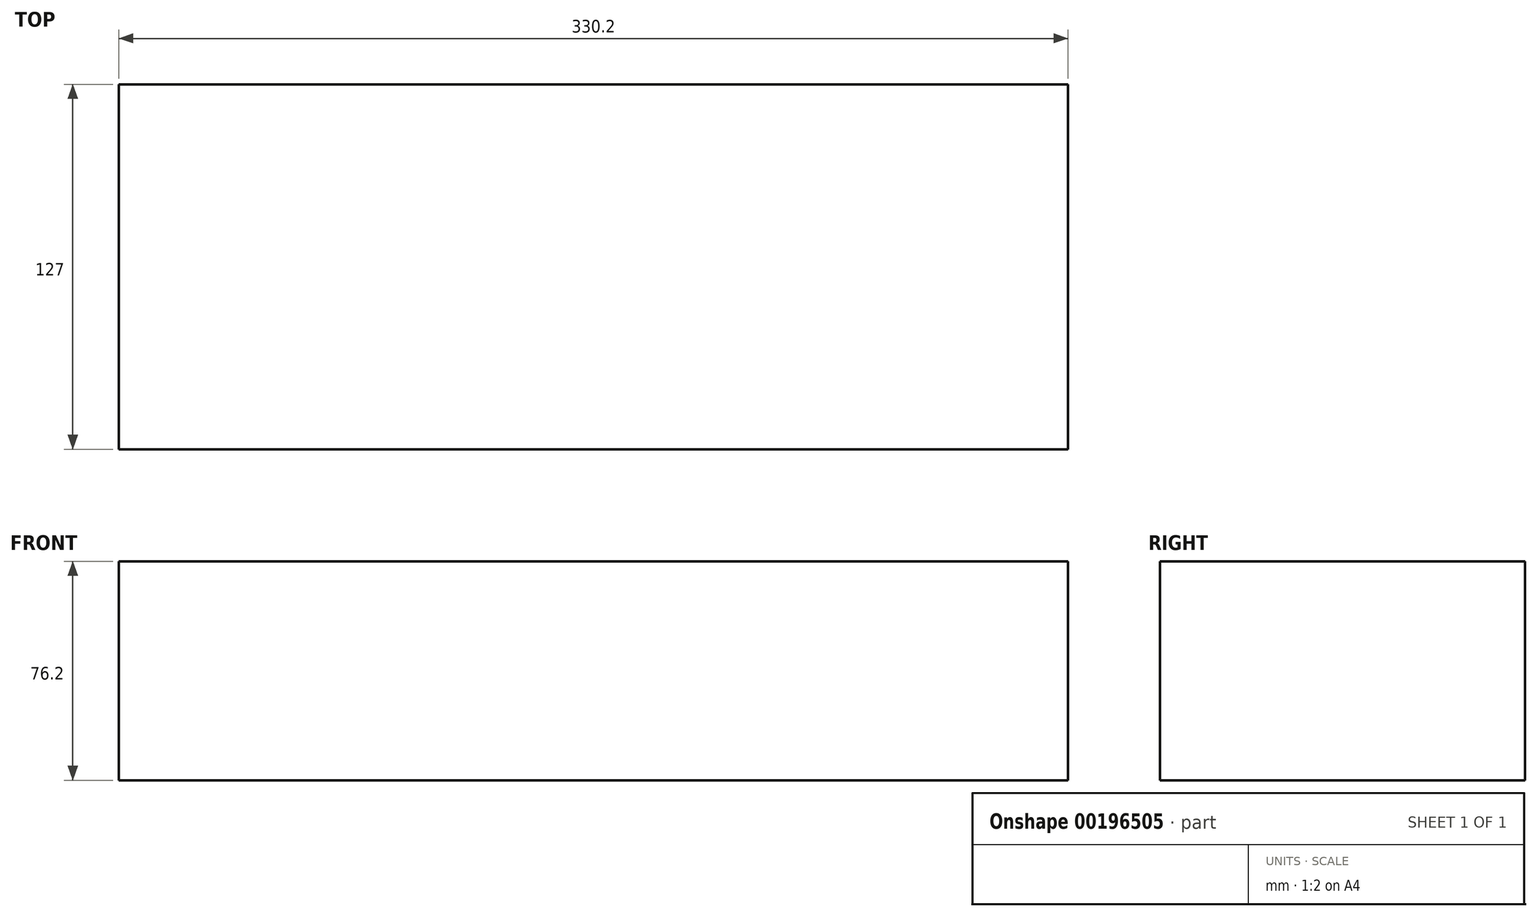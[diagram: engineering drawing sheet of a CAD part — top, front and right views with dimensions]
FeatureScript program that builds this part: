
annotation { "Feature Type Name" : "Feature", "Feature Type Description" : "" }
export const myFeature = defineFeature(function(context is Context, id is Id, definition is map)
    precondition{}
    {
        {
            var Q0;
            Q0=qCreatedBy(makeId("Front.planeOp"),FACE);
            var sketch = newSketch(context, id + "F0", { "sketchPlane" : qUnion([Q0])});
            skLineSegment(sketch, "E0.bottom", {"start": v(165.1, 38.1) * mm, "end": v(-165.1, 38.1) * mm});
            skLineSegment(sketch, "E0.top", {"start": v(165.1, -38.1) * mm, "end": v(-165.1, -38.1) * mm});
            skLineSegment(sketch, "E0.left", {"start": v(165.1, 38.1) * mm, "end": v(165.1, -38.1) * mm});
            skLineSegment(sketch, "E0.right", {"start": v(-165.1, 38.1) * mm, "end": v(-165.1, -38.1) * mm});
            skPoint(sketch, "E0.middle", {"position": v(0, 0) * mm});
            skSolve(sketch);
        }
        {
            var Q0;
            Q0 = qSketchRegion(id + "F0", true);
            extrude(context, id + "F1", {"entities" : qUnion([Q0]), "depth" : 63.5 * mm, "hasSecondDirection" : true, "secondDirectionOppositeDirection" : true, "secondDirectionDepth" : 63.5 * mm});
        }
    });
